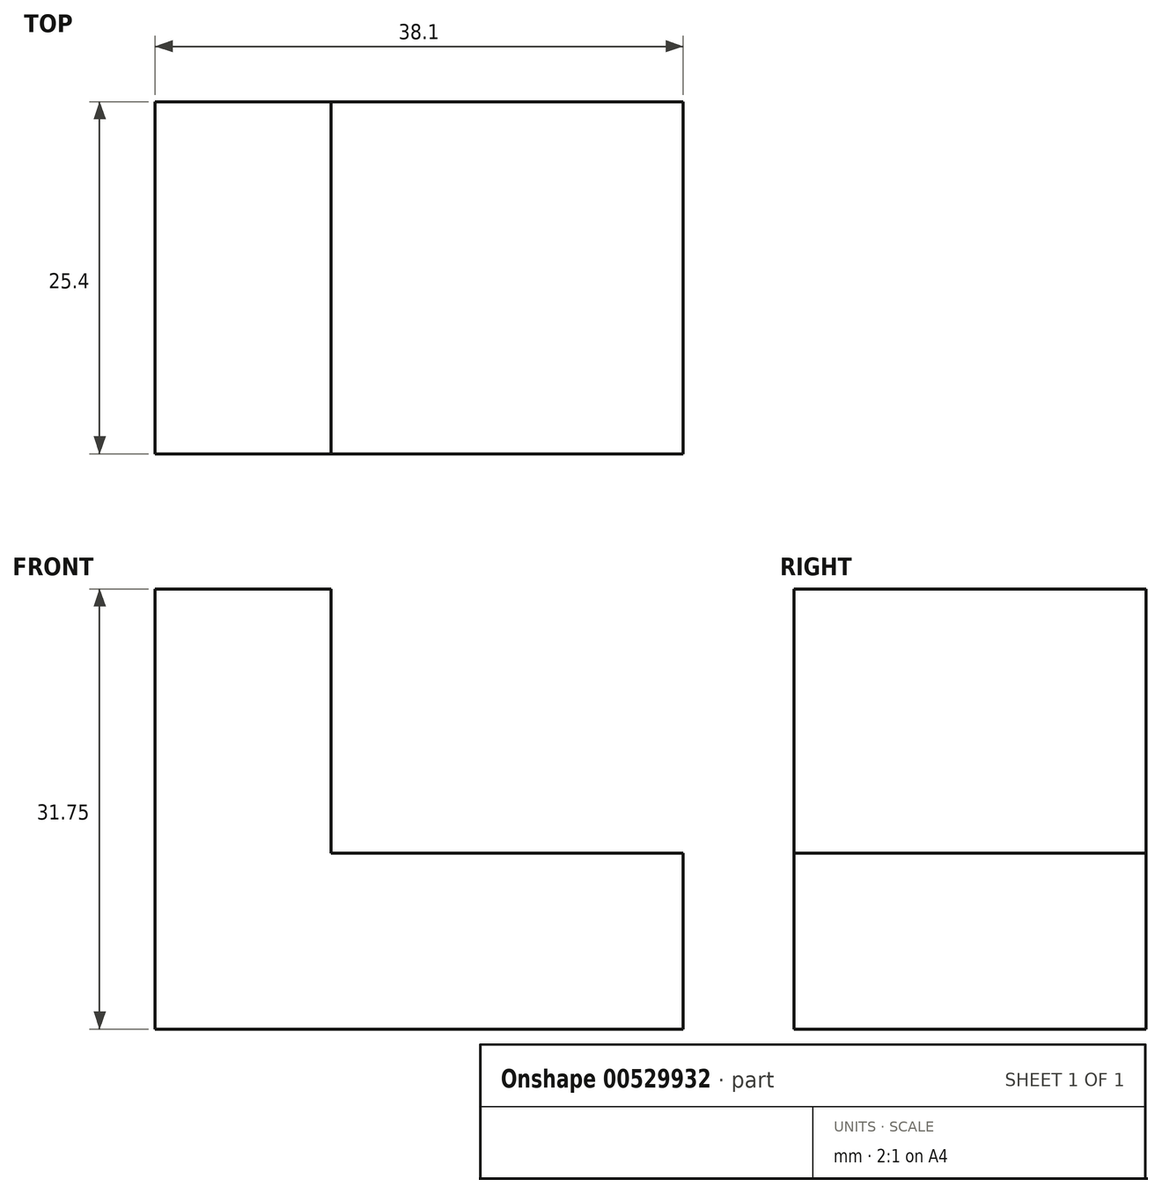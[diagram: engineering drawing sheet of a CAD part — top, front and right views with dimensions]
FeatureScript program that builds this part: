
annotation { "Feature Type Name" : "Feature", "Feature Type Description" : "" }
export const myFeature = defineFeature(function(context is Context, id is Id, definition is map)
    precondition{}
    {
        {
            var Q0;
            Q0=qCreatedBy(makeId("Front.planeOp"),FACE);
            var sketch = newSketch(context, id + "F0", { "sketchPlane" : qUnion([Q0])});
            skLineSegment(sketch, "E0", {"start": v(-64.46, 14.4) * mm, "end": v(-26.36, 14.4) * mm});
            skLineSegment(sketch, "E1", {"start": v(-26.36, 14.4) * mm, "end": v(-26.36, 27.1) * mm});
            skLineSegment(sketch, "E2", {"start": v(-26.36, 27.1) * mm, "end": v(-51.76, 27.1) * mm});
            skLineSegment(sketch, "E3", {"start": v(-51.76, 27.1) * mm, "end": v(-51.76, 46.15) * mm});
            skLineSegment(sketch, "E4", {"start": v(-51.76, 46.15) * mm, "end": v(-64.46, 46.15) * mm});
            skLineSegment(sketch, "E5", {"start": v(-64.46, 46.15) * mm, "end": v(-64.46, 14.4) * mm});
            skSolve(sketch);
        }
        {
            var Q0;
            Q0=makeQuery(id+"F0.imprint","IMPRINT",FACE,{"disambiguationData":[TD([[makeQuery(id+"F0.imprint","IMPRINT",EDGE,{"derivedFrom":sQuery(id+"F0.wireOp",EDGE,"E0")}),1.0]])]});
            extrude(context, id + "F1", {"entities" : qUnion([Q0]), "depth" : 25.4 * mm, "offsetDistance" : 25.4 * mm});
        }
    });
